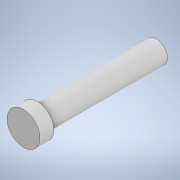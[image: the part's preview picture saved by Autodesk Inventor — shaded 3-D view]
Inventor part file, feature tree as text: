
AUTODESK INVENTOR PART (.ipt)
format: ipt  version: 2021 (Build 250183000, 183)  size: 100,352 bytes
history: native  units: mm
features: extrude x2, sketch x2
ambient origin geometry x8: Origin, YZ Plane, XZ Plane, XY Plane, X Axis, Y Axis, Z Axis, Center Point
bodies: Solid1 (feature_tree)
feature tree (4):
  extrude  "Extrusion1"  TaperAngle=0.0deg  [1 undecoded]
  extrude  "Extrusion2"  [1 undecoded]
  sketch  "Sketch1"  dims[d2=0.0mm d5=0.0mm]
  sketch  "Sketch2"
note: 2 required parameter values undecoded (feature->parameter linkage not recoverable at this tier; creation-order binding heuristic only, values carry confidence <= 0.55)
